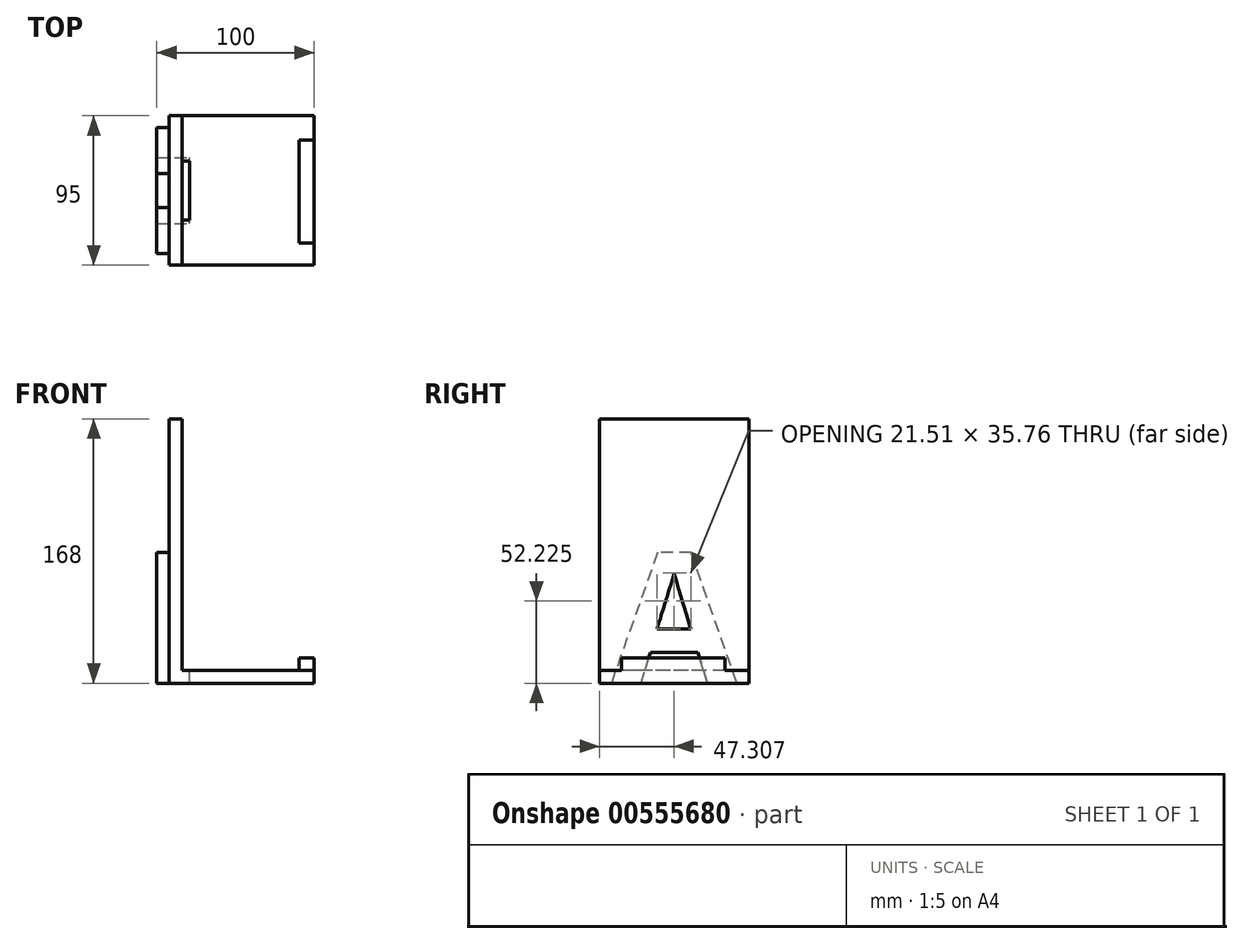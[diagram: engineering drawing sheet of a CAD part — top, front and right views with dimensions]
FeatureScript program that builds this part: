
annotation { "Feature Type Name" : "Feature", "Feature Type Description" : "" }
export const myFeature = defineFeature(function(context is Context, id is Id, definition is map)
    precondition{}
    {
        {
            var Q0;
            Q0=qCreatedBy(makeId("Top.planeOp"),FACE);
            var sketch = newSketch(context, id + "F0", { "sketchPlane" : qUnion([Q0])});
            skLineSegment(sketch, "E0.bottom", {"start": v(-46, -47.5) * mm, "end": v(46, -47.5) * mm});
            skLineSegment(sketch, "E0.top", {"start": v(-46, 47.5) * mm, "end": v(46, 47.5) * mm});
            skLineSegment(sketch, "E0.left", {"start": v(-46, -47.5) * mm, "end": v(-46, 47.5) * mm});
            skLineSegment(sketch, "E0.right", {"start": v(46, -47.5) * mm, "end": v(46, 47.5) * mm});
            skPoint(sketch, "E0.middle", {"position": v(0, 0) * mm});
            skSolve(sketch);
        }
        {
            var Q0;
            Q0=makeQuery(id+"F0.imprint","IMPRINT",FACE,{"disambiguationData":[TD([[makeQuery(id+"F0.imprint","IMPRINT",EDGE,{"derivedFrom":sQuery(id+"F0.wireOp",EDGE,"E0.bottom")}),1.0]])]});
            extrude(context, id + "F1", {"entities" : qUnion([Q0]), "depth" : 8 * mm, "offsetDistance" : 25 * mm});
        }
        {
            var Q0;
            Q0=makeQuery(id+"F1.opExtrude","CAP_FACE",FACE,{"disambiguationData":[OSD([sQuery(id+"F0.wireOp",EDGE,"E0.bottom"),sQuery(id+"F0.wireOp",EDGE,"E0.top"),sQuery(id+"F0.wireOp",EDGE,"E0.left"),sQuery(id+"F0.wireOp",EDGE,"E0.right")])],"isStart":false});
            var sketch = newSketch(context, id + "F2", { "sketchPlane" : qUnion([Q0])});
            skLineSegment(sketch, "E1.bottom", {"start": v(-46, 47.5) * mm, "end": v(-38, 47.5) * mm});
            skLineSegment(sketch, "E1.top", {"start": v(-46, -47.5) * mm, "end": v(-38, -47.5) * mm});
            skLineSegment(sketch, "E1.left", {"start": v(-46, 47.5) * mm, "end": v(-46, -47.5) * mm});
            skLineSegment(sketch, "E1.right", {"start": v(-38, 47.5) * mm, "end": v(-38, -47.5) * mm});
            skSolve(sketch);
        }
        {
            var Q0;
            Q0 = qSketchRegion(id + "F2", true);
            extrude(context, id + "F3", {"entities" : qUnion([Q0]), "operationType" : NewBodyOperationType.ADD, "depth" : 160 * mm, "offsetDistance" : 25 * mm});
        }
        {
            var Q0;
            Q0=makeQuery(id+"F1.opExtrude","CAP_FACE",FACE,{"disambiguationData":[OSD([sQuery(id+"F0.wireOp",EDGE,"E0.bottom"),sQuery(id+"F0.wireOp",EDGE,"E0.top"),sQuery(id+"F0.wireOp",EDGE,"E0.left"),sQuery(id+"F0.wireOp",EDGE,"E0.right")])],"isStart":false});
            var sketch = newSketch(context, id + "F4", { "sketchPlane" : qUnion([Q0])});
            skLineSegment(sketch, "E2.bottom", {"start": v(46, 32.06) * mm, "end": v(36.5, 32.06) * mm});
            skLineSegment(sketch, "E2.top", {"start": v(46, -33.37) * mm, "end": v(36.5, -33.37) * mm});
            skLineSegment(sketch, "E2.left", {"start": v(46, 32.06) * mm, "end": v(46, -33.37) * mm});
            skLineSegment(sketch, "E2.right", {"start": v(36.5, 32.06) * mm, "end": v(36.5, -33.37) * mm});
            skSolve(sketch);
        }
        {
            var Q0;
            Q0=makeQuery(id+"F4.imprint","IMPRINT",FACE,{"disambiguationData":[TD([[makeQuery(id+"F4.imprint","IMPRINT",EDGE,{"derivedFrom":sQuery(id+"F4.wireOp",EDGE,"E2.bottom")}),1.0]])]});
            extrude(context, id + "F5", {"entities" : qUnion([Q0]), "operationType" : NewBodyOperationType.ADD, "depth" : 8 * mm, "offsetDistance" : 25 * mm});
        }
        {
            var Q0;
            Q0=makeQuery(id+"F3.boolean.opBoolean","MERGE",FACE,{"derivedFrom":[makeQuery(id+"F1.opExtrude","SWEPT_FACE",FACE,{"disambiguationData":[OSD([sQuery(id+"F0.wireOp",EDGE,"E0.left")])]}),makeQuery(id+"F3.opExtrude","SWEPT_FACE",FACE,{"disambiguationData":[OSD([sQuery(id+"F2.wireOp",EDGE,"E1.left")])]})]});
            var sketch = newSketch(context, id + "F6", { "sketchPlane" : qUnion([Q0])});
            skText(sketch, "E3", { "text": "A", "fontName": "OpenSans-Bold.ttf"});
            const initialGuessF6  = {"E3": [-0.03983, 0, 1, 0, 0.0833]};
            skSetInitialGuess(sketch, initialGuessF6);
            skSolve(sketch);
        }
        {
            var Q0;
            Q0 = qSketchRegion(id + "F6", true);
            extrude(context, id + "F7", {"entities" : qUnion([Q0]), "operationType" : NewBodyOperationType.ADD, "depth" : 8 * mm, "offsetDistance" : 25 * mm});
        }
        {
            var Q0;
            Q0=makeQuery(id+"F7.boolean.opBoolean","SPLIT",FACE,{"disambiguationData":[TD([makeQuery(id+"F7.opExtrude","SWEPT_FACE",FACE,{"disambiguationData":[OSD([sQuery(id+"F6.wireOp",EDGE,"E3.sketch_text.stroke-8")])]})])],"derivedFrom":makeQuery(id+"F3.boolean.opBoolean","MERGE",FACE,{"derivedFrom":[makeQuery(id+"F1.opExtrude","SWEPT_FACE",FACE,{"disambiguationData":[OSD([sQuery(id+"F0.wireOp",EDGE,"E0.left")])]}),makeQuery(id+"F3.opExtrude","SWEPT_FACE",FACE,{"disambiguationData":[OSD([sQuery(id+"F2.wireOp",EDGE,"E1.left")])]})]})});
            var Q1;
            {var subQ0=sQuery(id+"F0.wireOp",EDGE,"E0.left");Q1=makeQuery(id+"F7.boolean.opBoolean","SPLIT",FACE,{"disambiguationData":[TD([makeQuery(id+"F7.opExtrude","SWEPT_FACE",FACE,{"disambiguationData":[OSD([sQuery(id+"F6.wireOp",EDGE,"E3.sketch_text.stroke-0")])]})])],"derivedFrom":makeQuery(id+"F3.boolean.opBoolean","MERGE",FACE,{"derivedFrom":[makeQuery(id+"F1.opExtrude","SWEPT_FACE",FACE,{"disambiguationData":[OSD([subQ0])]}),makeQuery(id+"F3.opExtrude","SWEPT_FACE",FACE,{"disambiguationData":[OSD([sQuery(id+"F2.wireOp",EDGE,"E1.left")])]})]})});}
            extrude(context, id + "F8", {"entities" : qUnion([Q0, Q1]), "operationType" : NewBodyOperationType.REMOVE, "oppositeDirection" : true, "depth" : 13 * mm, "offsetDistance" : 25 * mm});
        }
    });
